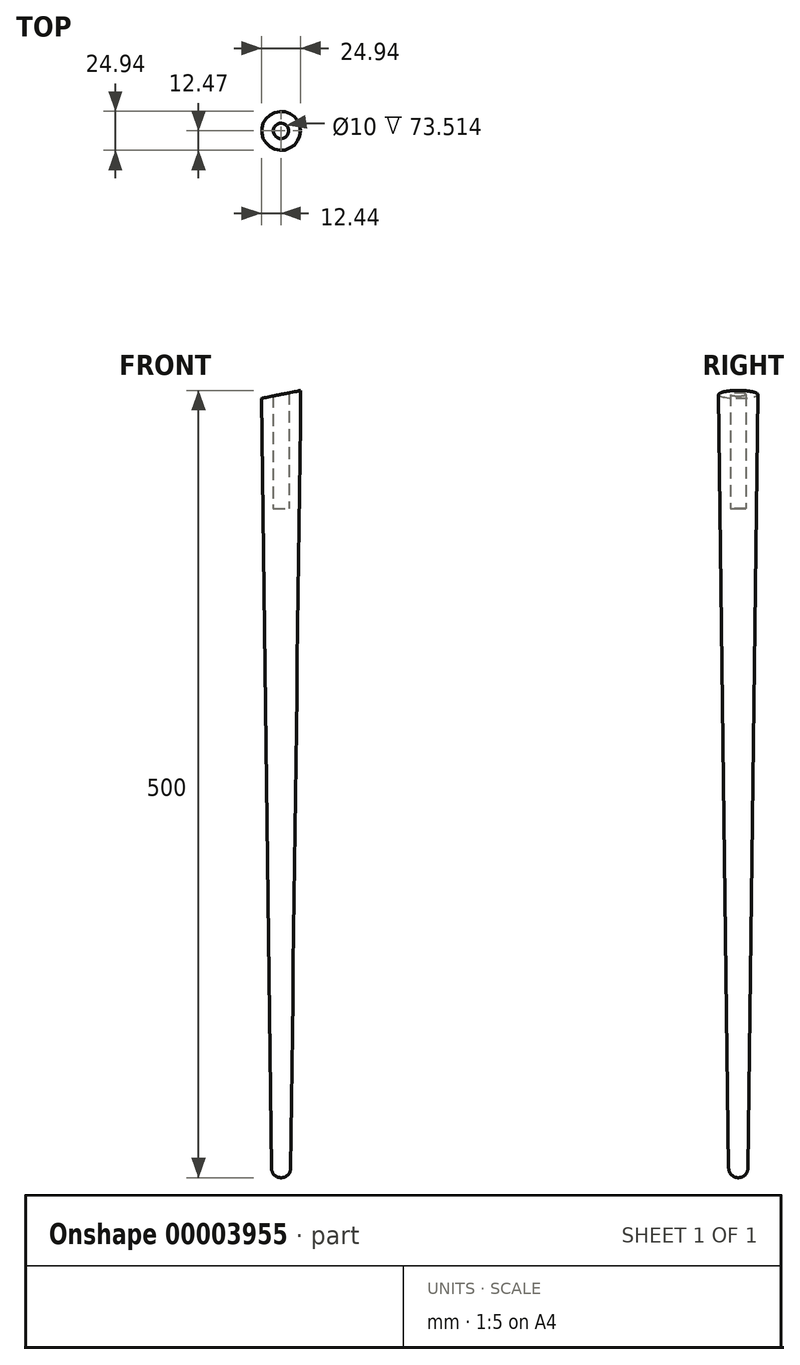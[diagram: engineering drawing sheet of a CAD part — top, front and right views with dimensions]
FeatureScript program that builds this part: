
annotation { "Feature Type Name" : "Feature", "Feature Type Description" : "" }
export const myFeature = defineFeature(function(context is Context, id is Id, definition is map)
    precondition{}
    {
        {
            var Q0;
            Q0=qCreatedBy(makeId("Front.planeOp"),FACE);
            var sketch = newSketch(context, id + "F0", { "sketchPlane" : qUnion([Q0])});
            skLineSegment(sketch, "E0", {"start": v(0, 0) * mm, "end": v(0, 425) * mm});
            skLineSegment(sketch, "E1", {"start": v(0, 425) * mm, "end": v(-5, 425) * mm});
            skLineSegment(sketch, "E2", {"start": v(-5, 425) * mm, "end": v(-5, 500) * mm});
            skLineSegment(sketch, "E3", {"start": v(-5, 500) * mm, "end": v(-12.5, 500) * mm});
            skLineSegment(sketch, "E4", {"start": v(-12.5, 500) * mm, "end": v(-6, 0) * mm});
            skLineSegment(sketch, "E5", {"start": v(-6, 0) * mm, "end": v(0, 0) * mm});
            skLineSegment(sketch, "E6", {"start": v(0, 0) * mm, "end": v(0, 500) * mm});
            skSolve(sketch);
        }
        {
            var Q0;
            {var subQ2=sQuery(id+"F0.wireOp",EDGE,"E1");Q0=makeQuery(id+"F0.imprint","IMPRINT",FACE,{"disambiguationData":[TD([[makeQuery(id+"F0.imprint","IMPRINT",EDGE,{"derivedFrom":subQ2}),1.0]])]});}
            var Q1;
            Q1=sQuery(id+"F0.wireOp",EDGE,"E6");
            revolve(context, id + "F1", {"entities" : qUnion([Q0]), "axis" : qUnion([Q1]), "revolveType" : RevolveType.FULL});
        }
        {
            var Q0;
            Q0=makeQuery(id+"F1.opRevolve","SWEPT_EDGE",EDGE,{"disambiguationData":[OSD([sQuery(id+"F0.wireOp",EDGE,"E4"),sQuery(id+"F0.wireOp",EDGE,"E5")])]});
            fillet(context, id + "F2", {"entities" : qUnion([Q0]), "radius" : 6 * mm, "tangentPropagation" : true, "allowEdgeOverflow" : false});
        }
        {
            var Q0;
            Q0=qCreatedBy(makeId("Front.planeOp"),FACE);
            var sketch = newSketch(context, id + "F3", { "sketchPlane" : qUnion([Q0])});
            skLineSegment(sketch, "E7.bottom", {"start": v(-12.5, 500) * mm, "end": v(12.5, 500) * mm});
            skLineSegment(sketch, "E7.left", {"start": v(-12.5, 500) * mm, "end": v(-12.5, 495) * mm});
            skLineSegment(sketch, "E8", {"start": v(-12.5, 495) * mm, "end": v(12.5, 500) * mm});
            skSolve(sketch);
        }
        {
            var Q0;
            Q0=makeQuery(id+"F3.imprint","IMPRINT",FACE,{"disambiguationData":[TD([[makeQuery(id+"F3.imprint","IMPRINT",EDGE,{"derivedFrom":sQuery(id+"F3.wireOp",EDGE,"E7.bottom")}),-1.0]])]});
            extrude(context, id + "F4", {"entities" : qUnion([Q0]), "operationType" : NewBodyOperationType.REMOVE, "endBound" : BoundingType.SYMMETRIC, "oppositeDirection" : true, "depth" : 25 * mm});
        }
    });
